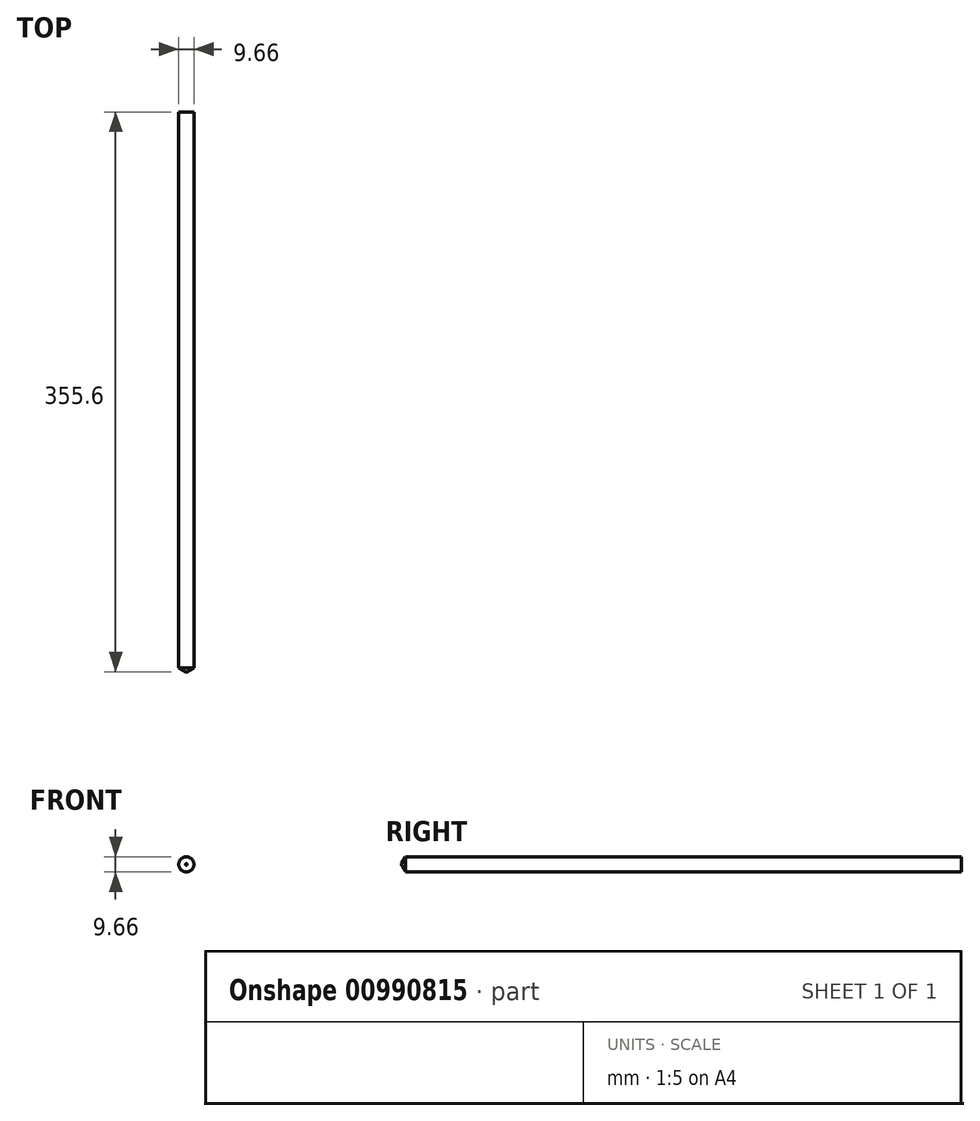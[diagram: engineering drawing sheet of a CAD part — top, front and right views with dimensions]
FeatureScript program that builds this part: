
annotation { "Feature Type Name" : "Feature", "Feature Type Description" : "" }
export const myFeature = defineFeature(function(context is Context, id is Id, definition is map)
    precondition{}
    {
        {
            var Q0;
            Q0=qCreatedBy(makeId("Front.planeOp"),FACE);
            var sketch = newSketch(context, id + "F0", { "sketchPlane" : qUnion([Q0])});
            skCircle(sketch, "E0", {"center": v(0, 0) * mm, "radius": 4.83 * mm});
            skSolve(sketch);
        }
        {
            var Q0;
            Q0 = qSketchRegion(id + "F0", true);
            extrude(context, id + "F1", {"entities" : qUnion([Q0]), "depth" : 355.6 * mm, "offsetDistance" : 25.4 * mm});
        }
        {
            var Q0;
            Q0=makeQuery(id+"F1.opExtrude","CAP_EDGE",EDGE,{"disambiguationData":[OSD([sQuery(id+"F0.wireOp",EDGE,"E0")])],"isStart":false});
            chamfer(context, id + "F2", {"entities" : qUnion([Q0]), "chamferType" : ChamferType.OFFSET_ANGLE, "width" : 4.32 * mm, "oppositeDirection" : false, "angle" : 31 * degree, "tangentPropagation" : true});
        }
    });
